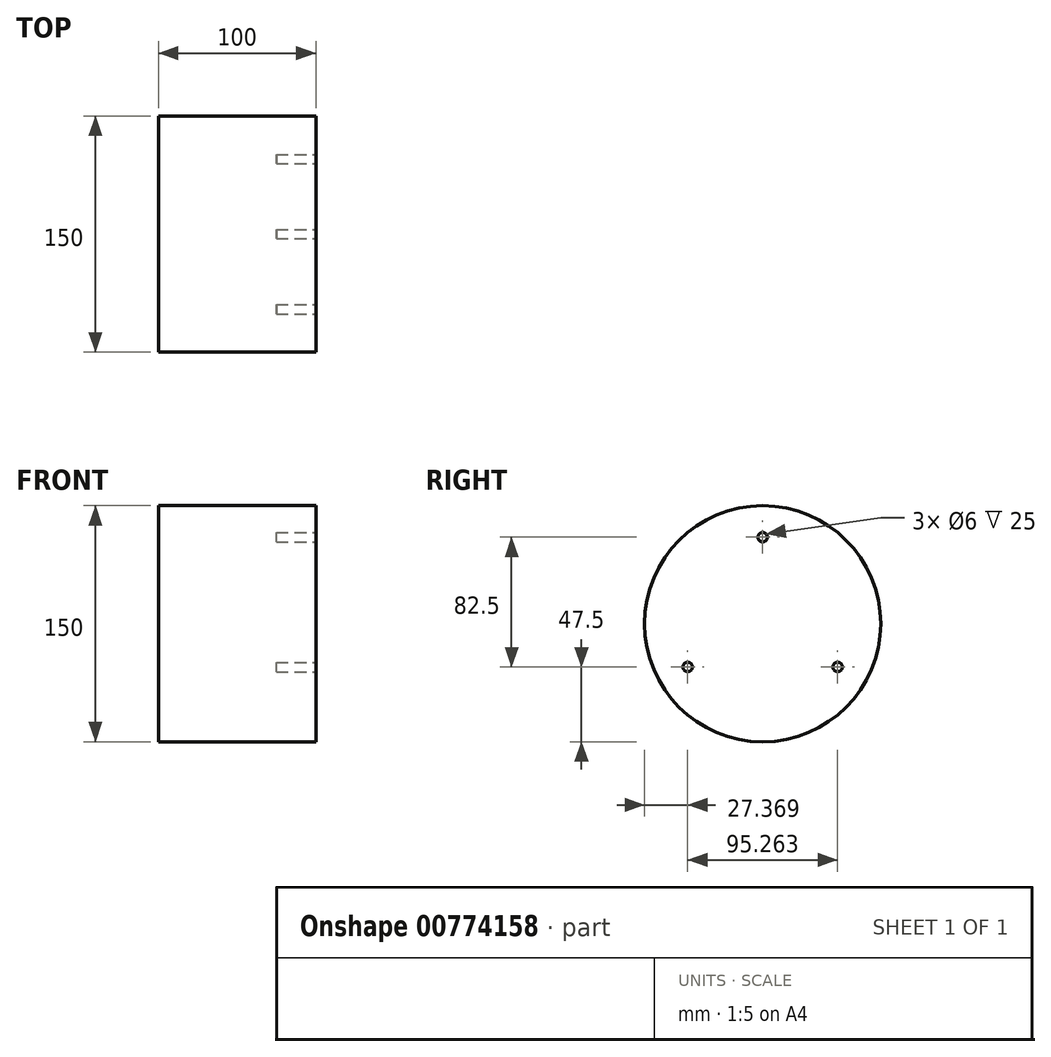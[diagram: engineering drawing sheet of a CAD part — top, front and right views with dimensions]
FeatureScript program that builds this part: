
annotation { "Feature Type Name" : "Feature", "Feature Type Description" : "" }
export const myFeature = defineFeature(function(context is Context, id is Id, definition is map)
    precondition{}
    {
        {
            var Q0;
            Q0=qCreatedBy(makeId("Front.planeOp"),FACE);
            var sketch = newSketch(context, id + "F0", { "sketchPlane" : qUnion([Q0])});
            skLineSegment(sketch, "E0.bottom", {"start": v(0, 0) * mm, "end": v(-100, 0) * mm});
            skLineSegment(sketch, "E0.top", {"start": v(0, -75) * mm, "end": v(-100, -75) * mm});
            skLineSegment(sketch, "E0.left", {"start": v(0, 0) * mm, "end": v(0, -75) * mm});
            skLineSegment(sketch, "E0.right", {"start": v(-100, 0) * mm, "end": v(-100, -75) * mm});
            skSolve(sketch);
        }
        {
            var Q0;
            Q0 = qSketchRegion(id + "F0", true);
            var Q1;
            Q1=sQuery(id+"F0.wireOp",EDGE,"E0.bottom");
            revolve(context, id + "F1", {"surfaceOperationType" : NewSurfaceOperationType.NEW, "entities" : qUnion([Q0]), "axis" : qUnion([Q1]), "revolveType" : RevolveType.FULL});
        }
        {
            var Q0;
            Q0=qCreatedBy(makeId("Right.planeOp"),FACE);
            var sketch = newSketch(context, id + "F2", { "sketchPlane" : qUnion([Q0])});
            skCircle(sketch, "E1", {"center": v(0, 55) * mm, "radius": 3 * mm});
            skCircle(sketch, "E2.1.0", {"center": v(-47.63, -27.5) * mm, "radius": 3 * mm});
            skCircle(sketch, "E2.2.0", {"center": v(47.63, -27.5) * mm, "radius": 3 * mm});
            skPoint(sketch, "E2.center", {"position": v(0, 0) * mm});
            skSolve(sketch);
        }
        {
            var Q0;
            Q0 = qSketchRegion(id + "F2", true);
            extrude(context, id + "F3", {"entities" : qUnion([Q0]), "operationType" : NewBodyOperationType.REMOVE, "oppositeDirection" : true, "depth" : 25 * mm, "offsetDistance" : 25 * mm});
        }
    });
